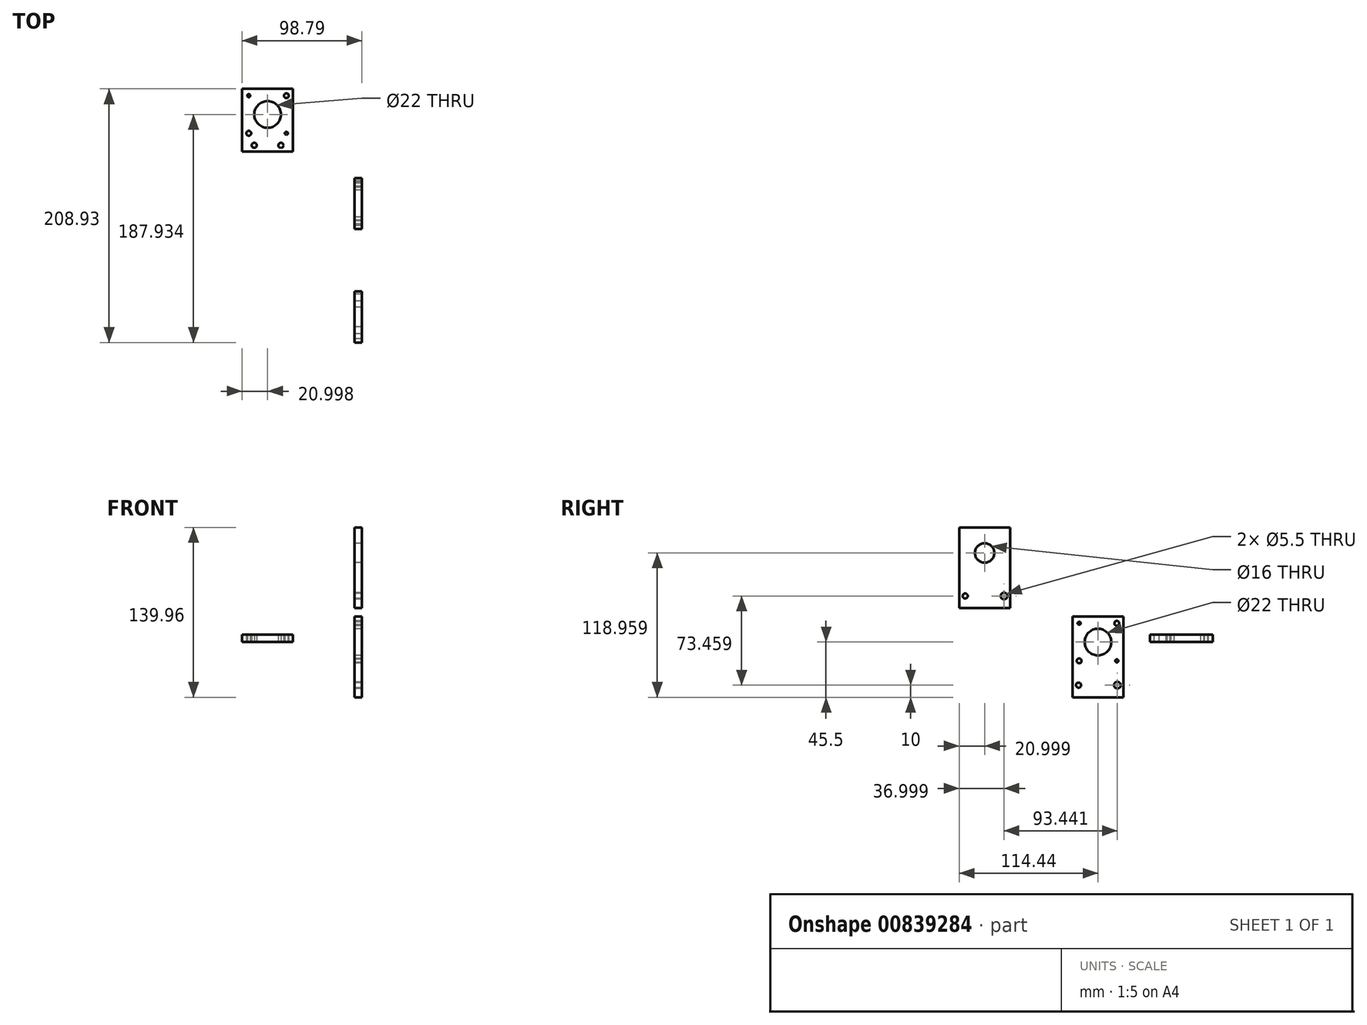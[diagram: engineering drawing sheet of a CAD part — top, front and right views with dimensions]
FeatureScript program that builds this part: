
annotation { "Feature Type Name" : "Feature", "Feature Type Description" : "" }
export const myFeature = defineFeature(function(context is Context, id is Id, definition is map)
    precondition{}
    {
        {
            var Q0;
            Q0=qCreatedBy(makeId("Right.planeOp"),FACE);
            var sketch = newSketch(context, id + "F0", { "sketchPlane" : qUnion([Q0])});
            skLineSegment(sketch, "E0.bottom", {"start": v(21, 21) * mm, "end": v(-21, 21) * mm});
            skLineSegment(sketch, "E0.top", {"start": v(21, -21) * mm, "end": v(-21, -21) * mm});
            skLineSegment(sketch, "E0.left", {"start": v(21, 21) * mm, "end": v(21, -21) * mm});
            skLineSegment(sketch, "E0.right", {"start": v(-21, 21) * mm, "end": v(-21, -21) * mm});
            skPoint(sketch, "E0.middle", {"position": v(0, 0) * mm});
            skCircle(sketch, "E1", {"center": v(-15.5, 15.5) * mm, "radius": 2 * mm});
            skCircle(sketch, "E2.MirrorC", {"center": v(15.5, 15.5) * mm, "radius": 2 * mm});
            skCircle(sketch, "E3.MirrorC", {"center": v(15.5, -15.5) * mm, "radius": 2 * mm});
            skCircle(sketch, "E4.MirrorC", {"center": v(-15.5, -15.5) * mm, "radius": 2 * mm});
            skCircle(sketch, "E5", {"center": v(0, 0) * mm, "radius": 11 * mm});
            skLineSegment(sketch, "E6", {"start": v(21, 0) * mm, "end": v(21, -25.5) * mm});
            skLineSegment(sketch, "E7.MirrorCS", {"start": v(-21, 0) * mm, "end": v(-21, -25.5) * mm});
            skLineSegment(sketch, "E8", {"start": v(-21, -25.5) * mm, "end": v(21, -25.5) * mm});
            skLineSegment(sketch, "E9.top", {"start": v(-21, -45.5) * mm, "end": v(21, -45.5) * mm});
            skLineSegment(sketch, "E9.left", {"start": v(-21, -25.5) * mm, "end": v(-21, -45.5) * mm});
            skLineSegment(sketch, "E9.right", {"start": v(21, -25.5) * mm, "end": v(21, -45.5) * mm});
            skCircle(sketch, "E10", {"center": v(-16, -35.5) * mm, "radius": 2.75 * mm});
            skPoint(sketch, "E10.centerSnap0", {"position": v(-21, -35.5) * mm});
            skCircle(sketch, "E11.MirrorC", {"center": v(16, -35.5) * mm, "radius": 2.75 * mm});
            skSolve(sketch);
        }
        {
            var Q0;
            {var subQ0=sQuery(id+"F0.wireOp",EDGE,"E0.top");Q0=makeQuery(id+"F0.imprint","IMPRINT",FACE,{"disambiguationData":[TD([[makeQuery(id+"F0.imprint","IMPRINT",EDGE,{"derivedFrom":subQ0}),1.0]])]});}
            var Q1;
            Q1=makeQuery(id+"F0.imprint","IMPRINT",FACE,{"disambiguationData":[TD([[makeQuery(id+"F0.imprint","IMPRINT",EDGE,{"derivedFrom":sQuery(id+"F0.wireOp",EDGE,"E8")}),-1.0]])]});
            var Q2;
            Q2=makeQuery(id+"F0.imprint","IMPRINT",FACE,{"disambiguationData":[TD([[makeQuery(id+"F0.imprint","IMPRINT",EDGE,{"derivedFrom":sQuery(id+"F0.wireOp",EDGE,"E1")}),1.0]])]});
            var Q3;
            Q3=makeQuery(id+"F0.imprint","IMPRINT",FACE,{"disambiguationData":[TD([[makeQuery(id+"F0.imprint","IMPRINT",EDGE,{"derivedFrom":sQuery(id+"F0.wireOp",EDGE,"E0.bottom")}),1.0]])]});
            var Q4;
            Q4=makeQuery(id+"F0.imprint","IMPRINT",FACE,{"disambiguationData":[TD([[makeQuery(id+"F0.imprint","IMPRINT",EDGE,{"derivedFrom":sQuery(id+"F0.wireOp",EDGE,"E2.MirrorC")}),-1.0]])]});
            var Q5;
            Q5=makeQuery(id+"F0.imprint","IMPRINT",FACE,{"disambiguationData":[TD([[makeQuery(id+"F0.imprint","IMPRINT",EDGE,{"derivedFrom":sQuery(id+"F0.wireOp",EDGE,"E3.MirrorC")}),1.0]])]});
            var Q6;
            Q6=makeQuery(id+"F0.imprint","IMPRINT",FACE,{"disambiguationData":[TD([[makeQuery(id+"F0.imprint","IMPRINT",EDGE,{"derivedFrom":sQuery(id+"F0.wireOp",EDGE,"E4.MirrorC")}),-1.0]])]});
            var Q7;
            Q7=makeQuery(id+"F0.imprint","IMPRINT",FACE,{"disambiguationData":[TD([[makeQuery(id+"F0.imprint","IMPRINT",EDGE,{"derivedFrom":sQuery(id+"F0.wireOp",EDGE,"E10")}),1.0]])]});
            var Q8;
            Q8=makeQuery(id+"F0.imprint","IMPRINT",FACE,{"disambiguationData":[TD([[makeQuery(id+"F0.imprint","IMPRINT",EDGE,{"derivedFrom":sQuery(id+"F0.wireOp",EDGE,"E11.MirrorC")}),-1.0]])]});
            extrude(context, id + "F1", {"entities" : qUnion([Q0, Q1, Q2, Q3, Q4, Q5, Q6, Q7, Q8]), "depth" : 6 * mm, "offsetDistance" : 25 * mm});
        }
        {
            var Q0;
            Q0=qCreatedBy(makeId("Right.planeOp"),FACE);
            var sketch = newSketch(context, id + "F2", { "sketchPlane" : qUnion([Q0])});
            skLineSegment(sketch, "E12.bottom", {"start": v(-72.44, 94.46) * mm, "end": v(-114.44, 94.46) * mm});
            skLineSegment(sketch, "E12.top", {"start": v(-72.44, 52.46) * mm, "end": v(-114.44, 52.46) * mm});
            skLineSegment(sketch, "E12.left", {"start": v(-72.44, 94.46) * mm, "end": v(-72.44, 52.46) * mm});
            skLineSegment(sketch, "E12.right", {"start": v(-114.44, 94.46) * mm, "end": v(-114.44, 52.46) * mm});
            skPoint(sketch, "E12.middle", {"position": v(-93.44, 73.46) * mm});
            skCircle(sketch, "E13", {"center": v(-93.44, 73.46) * mm, "radius": 8 * mm});
            skLineSegment(sketch, "E14", {"start": v(-72.44, 73.46) * mm, "end": v(-72.44, 47.96) * mm});
            skLineSegment(sketch, "E15.MirrorCS", {"start": v(-114.44, 73.46) * mm, "end": v(-114.44, 47.96) * mm});
            skLineSegment(sketch, "E16", {"start": v(-114.44, 47.96) * mm, "end": v(-72.44, 47.96) * mm});
            skLineSegment(sketch, "E17.top", {"start": v(-114.44, 27.96) * mm, "end": v(-72.44, 27.96) * mm});
            skLineSegment(sketch, "E17.left", {"start": v(-114.44, 47.96) * mm, "end": v(-114.44, 27.96) * mm});
            skLineSegment(sketch, "E17.right", {"start": v(-72.44, 47.96) * mm, "end": v(-72.44, 27.96) * mm});
            skCircle(sketch, "E18", {"center": v(-109.44, 37.96) * mm, "radius": 2.75 * mm});
            skPoint(sketch, "E18.centerSnap0", {"position": v(-114.44, 37.96) * mm});
            skCircle(sketch, "E19.MirrorC", {"center": v(-77.44, 37.96) * mm, "radius": 2.75 * mm});
            skSolve(sketch);
        }
        {
            var Q0;
            Q0=makeQuery(id+"F2.imprint","IMPRINT",FACE,{"disambiguationData":[TD([[makeQuery(id+"F2.imprint","IMPRINT",EDGE,{"derivedFrom":sQuery(id+"F2.wireOp",EDGE,"E12.bottom")}),1.0]])]});
            var Q1;
            {var subQ0=sQuery(id+"F2.wireOp",EDGE,"E12.top");Q1=makeQuery(id+"F2.imprint","IMPRINT",FACE,{"disambiguationData":[TD([[makeQuery(id+"F2.imprint","IMPRINT",EDGE,{"derivedFrom":subQ0}),1.0]])]});}
            var Q2;
            Q2=makeQuery(id+"F2.imprint","IMPRINT",FACE,{"disambiguationData":[TD([[makeQuery(id+"F2.imprint","IMPRINT",EDGE,{"derivedFrom":sQuery(id+"F2.wireOp",EDGE,"E16")}),-1.0]])]});
            var Q3;
            Q3=makeQuery(id+"F2.imprint","IMPRINT",FACE,{"disambiguationData":[TD([[makeQuery(id+"F2.imprint","IMPRINT",EDGE,{"derivedFrom":sQuery(id+"F2.wireOp",EDGE,"E18")}),1.0]])]});
            var Q4;
            Q4=makeQuery(id+"F2.imprint","IMPRINT",FACE,{"disambiguationData":[TD([[makeQuery(id+"F2.imprint","IMPRINT",EDGE,{"derivedFrom":sQuery(id+"F2.wireOp",EDGE,"E19.MirrorC")}),-1.0]])]});
            extrude(context, id + "F3", {"entities" : qUnion([Q0, Q1, Q2, Q3, Q4]), "depth" : 6 * mm, "offsetDistance" : 25 * mm});
        }
        {
            var Q0;
            Q0=sQuery(id+"F0.wireOp",VERTEX,"E1.center");
            var Q1;
            Q1=sQuery(id+"F0.wireOp",VERTEX,"E2.MirrorC.center");
            var Q2;
            Q2=sQuery(id+"F0.wireOp",VERTEX,"E4.MirrorC.center");
            var Q3;
            Q3=sQuery(id+"F0.wireOp",VERTEX,"E3.MirrorC.center");
            var Q4;
            Q4=makeQuery(id+"F1.opExtrude","SWEPT_BODY",BODY,{"disambiguationData":[OSD([sQuery(id+"F0.wireOp",EDGE,"E0.bottom"),sQuery(id+"F0.wireOp",EDGE,"E0.left"),sQuery(id+"F0.wireOp",EDGE,"E0.right"),sQuery(id+"F0.wireOp",EDGE,"E5"),sQuery(id+"F0.wireOp",EDGE,"E6"),sQuery(id+"F0.wireOp",EDGE,"E7.MirrorCS"),sQuery(id+"F0.wireOp",EDGE,"E9.top"),sQuery(id+"F0.wireOp",EDGE,"E9.left"),sQuery(id+"F0.wireOp",EDGE,"E9.right")])]});
            hole(context, id + "F4", {"style" : HoleStyle.SIMPLE, "endStyle" : HoleEndStyle.THROUGH, "oppositeDirection" : true, "standardTappedOrClearance" : lookupTablePath({ "standard" : "ISO", "engagement" : "75%", "pitch" : "0.5 mm", "size" : "M3", "type" : "Tapped" }), "standardBlindInLast" : lookupTablePath({ "standard" : "ISO", "fit" : "Normal", "engagement" : "75%", "pitch" : "0.5 mm", "size" : "M3", "type" : "Clearance & tapped" }), "holeDiameter" : 2.5 * mm, "majorDiameter" : 3 * mm, "showTappedDepth" : true, "isTappedThrough" : true, "tappedDepth" : 12 * mm, "tapClearance" : 3, "locations" : qUnion([Q0, Q1, Q2, Q3]), "scope" : qUnion([Q4])});
        }
        {
            var Q0;
            Q0=sQuery(id+"F0.wireOp",VERTEX,"E10.center");
            var Q1;
            Q1=sQuery(id+"F0.wireOp",VERTEX,"E11.MirrorC.center");
            var Q2;
            Q2=makeQuery(id+"F1.opExtrude","SWEPT_BODY",BODY,{"disambiguationData":[OSD([sQuery(id+"F0.wireOp",EDGE,"E0.bottom"),sQuery(id+"F0.wireOp",EDGE,"E0.left"),sQuery(id+"F0.wireOp",EDGE,"E0.right"),sQuery(id+"F0.wireOp",EDGE,"E5"),sQuery(id+"F0.wireOp",EDGE,"E6"),sQuery(id+"F0.wireOp",EDGE,"E7.MirrorCS"),sQuery(id+"F0.wireOp",EDGE,"E9.top"),sQuery(id+"F0.wireOp",EDGE,"E9.left"),sQuery(id+"F0.wireOp",EDGE,"E9.right")])]});
            hole(context, id + "F5", {"style" : HoleStyle.SIMPLE, "endStyle" : HoleEndStyle.THROUGH, "oppositeDirection" : true, "standardTappedOrClearance" : lookupTablePath({ "standard" : "ISO", "engagement" : "75%", "pitch" : "0.8 mm", "size" : "M5", "type" : "Tapped" }), "standardBlindInLast" : lookupTablePath({ "standard" : "ISO", "fit" : "Normal", "engagement" : "75%", "pitch" : "0.8 mm", "size" : "M5", "type" : "Clearance & tapped" }), "holeDiameter" : 4.2 * mm, "majorDiameter" : 5 * mm, "showTappedDepth" : true, "isTappedThrough" : true, "tappedDepth" : 12 * mm, "tapClearance" : 3, "locations" : qUnion([Q0, Q1]), "scope" : qUnion([Q2])});
        }
        {
            var Q0;
            Q0=sQuery(id+"F2.wireOp",VERTEX,"E18.center");
            var Q1;
            Q1=sQuery(id+"F2.wireOp",VERTEX,"E19.MirrorC.center");
            var Q2;
            Q2=makeQuery(id+"F3.opExtrude","SWEPT_BODY",BODY,{"disambiguationData":[OSD([sQuery(id+"F2.wireOp",EDGE,"E12.bottom"),sQuery(id+"F2.wireOp",EDGE,"E12.left"),sQuery(id+"F2.wireOp",EDGE,"E12.right"),sQuery(id+"F2.wireOp",EDGE,"E13"),sQuery(id+"F2.wireOp",EDGE,"E14"),sQuery(id+"F2.wireOp",EDGE,"E15.MirrorCS"),sQuery(id+"F2.wireOp",EDGE,"E17.top"),sQuery(id+"F2.wireOp",EDGE,"E17.left"),sQuery(id+"F2.wireOp",EDGE,"E17.right")])]});
            hole(context, id + "F6", {"style" : HoleStyle.SIMPLE, "endStyle" : HoleEndStyle.THROUGH, "oppositeDirection" : true, "standardTappedOrClearance" : lookupTablePath({ "standard" : "ISO", "engagement" : "75%", "pitch" : "0.8 mm", "size" : "M5", "type" : "Tapped" }), "standardBlindInLast" : lookupTablePath({ "standard" : "ISO", "fit" : "Normal", "engagement" : "75%", "pitch" : "0.8 mm", "size" : "M5", "type" : "Clearance & tapped" }), "holeDiameter" : 4.2 * mm, "majorDiameter" : 5 * mm, "showTappedDepth" : true, "isTappedThrough" : true, "tappedDepth" : 12 * mm, "tapClearance" : 3, "locations" : qUnion([Q0, Q1]), "scope" : qUnion([Q2])});
        }
        {
            var Q0;
            Q0=qCreatedBy(makeId("Top.planeOp"),FACE);
            var sketch = newSketch(context, id + "F7", { "sketchPlane" : qUnion([Q0])});
            skLineSegment(sketch, "E20.bottom", {"start": v(-50.8, 94.5) * mm, "end": v(-92.8, 94.5) * mm});
            skLineSegment(sketch, "E20.top", {"start": v(-50.8, 52.5) * mm, "end": v(-92.8, 52.5) * mm});
            skLineSegment(sketch, "E20.left", {"start": v(-50.8, 94.5) * mm, "end": v(-50.8, 52.5) * mm});
            skLineSegment(sketch, "E20.right", {"start": v(-92.8, 94.5) * mm, "end": v(-92.8, 52.5) * mm});
            skPoint(sketch, "E20.middle", {"position": v(-71.8, 73.5) * mm});
            skCircle(sketch, "E21", {"center": v(-87.3, 88.93) * mm, "radius": 2 * mm});
            skCircle(sketch, "E22.MirrorC", {"center": v(-56.3, 88.93) * mm, "radius": 2 * mm});
            skCircle(sketch, "E23.MirrorC", {"center": v(-56.3, 57.93) * mm, "radius": 2 * mm});
            skCircle(sketch, "E24.MirrorC", {"center": v(-87.3, 57.93) * mm, "radius": 2 * mm});
            skCircle(sketch, "E25", {"center": v(-71.8, 73.5) * mm, "radius": 11 * mm});
            skLineSegment(sketch, "E26", {"start": v(-92.8, 52.5) * mm, "end": v(-92.8, 43) * mm});
            skLineSegment(sketch, "E27", {"start": v(-92.8, 43) * mm, "end": v(-50.8, 43) * mm});
            skLineSegment(sketch, "E28", {"start": v(-50.8, 43) * mm, "end": v(-50.8, 52.5) * mm});
            skSolve(sketch);
        }
        {
            var Q0;
            Q0=makeQuery(id+"F7.imprint","IMPRINT",FACE,{"disambiguationData":[TD([[makeQuery(id+"F7.imprint","IMPRINT",EDGE,{"derivedFrom":sQuery(id+"F7.wireOp",EDGE,"E20.bottom")}),1.0]])]});
            var Q1;
            Q1=makeQuery(id+"F7.imprint","IMPRINT",FACE,{"disambiguationData":[TD([[makeQuery(id+"F7.imprint","IMPRINT",EDGE,{"derivedFrom":sQuery(id+"F7.wireOp",EDGE,"E20.top")}),1.0]])]});
            var Q2;
            Q2=makeQuery(id+"F7.imprint","IMPRINT",FACE,{"disambiguationData":[TD([[makeQuery(id+"F7.imprint","IMPRINT",EDGE,{"derivedFrom":sQuery(id+"F7.wireOp",EDGE,"E21")}),1.0]])]});
            var Q3;
            Q3=makeQuery(id+"F7.imprint","IMPRINT",FACE,{"disambiguationData":[TD([[makeQuery(id+"F7.imprint","IMPRINT",EDGE,{"derivedFrom":sQuery(id+"F7.wireOp",EDGE,"E22.MirrorC")}),-1.0]])]});
            var Q4;
            Q4=makeQuery(id+"F7.imprint","IMPRINT",FACE,{"disambiguationData":[TD([[makeQuery(id+"F7.imprint","IMPRINT",EDGE,{"derivedFrom":sQuery(id+"F7.wireOp",EDGE,"E23.MirrorC")}),1.0]])]});
            var Q5;
            Q5=makeQuery(id+"F7.imprint","IMPRINT",FACE,{"disambiguationData":[TD([[makeQuery(id+"F7.imprint","IMPRINT",EDGE,{"derivedFrom":sQuery(id+"F7.wireOp",EDGE,"E24.MirrorC")}),-1.0]])]});
            extrude(context, id + "F8", {"entities" : qUnion([Q0, Q1, Q2, Q3, Q4, Q5]), "depth" : 6 * mm, "offsetDistance" : 25 * mm});
        }
        {
            var Q0;
            Q0=sQuery(id+"F7.wireOp",VERTEX,"E22.MirrorC.center");
            var Q1;
            Q1=sQuery(id+"F7.wireOp",VERTEX,"E21.center");
            var Q2;
            Q2=sQuery(id+"F7.wireOp",VERTEX,"E23.MirrorC.center");
            var Q3;
            Q3=sQuery(id+"F7.wireOp",VERTEX,"E24.MirrorC.center");
            var Q4;
            Q4=makeQuery(id+"F8.opExtrude","SWEPT_BODY",BODY,{"disambiguationData":[OSD([sQuery(id+"F7.wireOp",EDGE,"E20.bottom"),sQuery(id+"F7.wireOp",EDGE,"E20.left"),sQuery(id+"F7.wireOp",EDGE,"E20.right"),sQuery(id+"F7.wireOp",EDGE,"E25"),sQuery(id+"F7.wireOp",EDGE,"E26"),sQuery(id+"F7.wireOp",EDGE,"E27"),sQuery(id+"F7.wireOp",EDGE,"E28")])]});
            hole(context, id + "F9", {"style" : HoleStyle.SIMPLE, "endStyle" : HoleEndStyle.THROUGH, "oppositeDirection" : true, "standardTappedOrClearance" : lookupTablePath({ "standard" : "ISO", "engagement" : "75%", "pitch" : "0.5 mm", "size" : "M3", "type" : "Tapped" }), "standardBlindInLast" : lookupTablePath({ "standard" : "ISO", "fit" : "Normal", "engagement" : "75%", "pitch" : "0.5 mm", "size" : "M3", "type" : "Clearance & tapped" }), "holeDiameter" : 2.5 * mm, "majorDiameter" : 3 * mm, "showTappedDepth" : true, "isTappedThrough" : true, "tappedDepth" : 10 * mm, "tapClearance" : 3, "locations" : qUnion([Q0, Q1, Q2, Q3]), "scope" : qUnion([Q4])});
        }
        {
            var Q0;
            Q0=makeQuery(id+"F8.opExtrude","CAP_FACE",FACE,{"disambiguationData":[OSD([sQuery(id+"F7.wireOp",EDGE,"E20.bottom"),sQuery(id+"F7.wireOp",EDGE,"E20.left"),sQuery(id+"F7.wireOp",EDGE,"E20.right"),sQuery(id+"F7.wireOp",EDGE,"E25"),sQuery(id+"F7.wireOp",EDGE,"E26"),sQuery(id+"F7.wireOp",EDGE,"E27"),sQuery(id+"F7.wireOp",EDGE,"E28")])],"isStart":true});
            var sketch = newSketch(context, id + "F10", { "sketchPlane" : qUnion([Q0])});
            skPoint(sketch, "E29", {"position": v(-60.8, -48) * mm});
            skPoint(sketch, "E30", {"position": v(-82.8, -48) * mm});
            skSolve(sketch);
        }
        {
            var Q0;
            Q0=sQuery(id+"F10.wireOp",VERTEX,"E29");
            var Q1;
            Q1=sQuery(id+"F10.wireOp",VERTEX,"E30");
            var Q2;
            Q2=makeQuery(id+"F8.opExtrude","SWEPT_BODY",BODY,{"disambiguationData":[OSD([sQuery(id+"F7.wireOp",EDGE,"E20.bottom"),sQuery(id+"F7.wireOp",EDGE,"E20.left"),sQuery(id+"F7.wireOp",EDGE,"E20.right"),sQuery(id+"F7.wireOp",EDGE,"E25"),sQuery(id+"F7.wireOp",EDGE,"E26"),sQuery(id+"F7.wireOp",EDGE,"E27"),sQuery(id+"F7.wireOp",EDGE,"E28")])]});
            hole(context, id + "F11", {"style" : HoleStyle.SIMPLE, "endStyle" : HoleEndStyle.THROUGH, "standardTappedOrClearance" : lookupTablePath({ "standard" : "ISO", "engagement" : "75%", "pitch" : "0.8 mm", "size" : "M5", "type" : "Tapped" }), "standardBlindInLast" : lookupTablePath({ "standard" : "ISO", "fit" : "Normal", "engagement" : "75%", "pitch" : "0.8 mm", "size" : "M5", "type" : "Clearance & tapped" }), "holeDiameter" : 4.2 * mm, "majorDiameter" : 5 * mm, "showTappedDepth" : true, "isTappedThrough" : true, "tappedDepth" : 10 * mm, "tapClearance" : 3, "locations" : qUnion([Q0, Q1]), "scope" : qUnion([Q2])});
        }
    });
